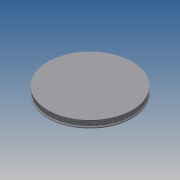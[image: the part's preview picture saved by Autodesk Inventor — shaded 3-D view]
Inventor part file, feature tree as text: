
AUTODESK INVENTOR PART (.ipt)
format: ipt  version: 2013 (Build 170138000, 138)  size: 691,712 bytes
history: native  units: mm
features: extrude x3, sketch x2, pattern_circular x1, chamfer x1, mirror x1
ambient origin geometry x8: Origin, YZ Plane, XZ Plane, XY Plane, X Axis, Y Axis, Z Axis, Center Point
bodies: Solid1 (feature_tree), Solid2 (feature_tree)
feature tree (8):
  extrude  "Extrusion14"  TaperAngle=360.0deg  [1 undecoded]
  extrude  "Extrusion15"  Depth=1.0mm TaperAngle=45.0deg
  pattern_circular  "Circular Pattern1"  [2 undecoded]
  extrude  "Extrusion3"  Depth=8.0mm TaperAngle=0.0deg
  chamfer  "Chamfer2"  Distance=1.59mm
  mirror  "Mirror1"
  sketch  "Sketch17"  dims[d11=0.254mm d20=2350.0mm d21=360.0deg]
  sketch  "Sketch18"  dims[d32=2.5mm d33=0.0mm d34=1.0mm d35=2.0mm d36=45.0deg d107=149.097647mm d110=8.0mm d111=0.0mm d112=1.59mm d114=8.0mm d115=0.0mm d116=1.0mm]
note: 3 required parameter values undecoded (feature->parameter linkage not recoverable at this tier; creation-order binding heuristic only, values carry confidence <= 0.55)
